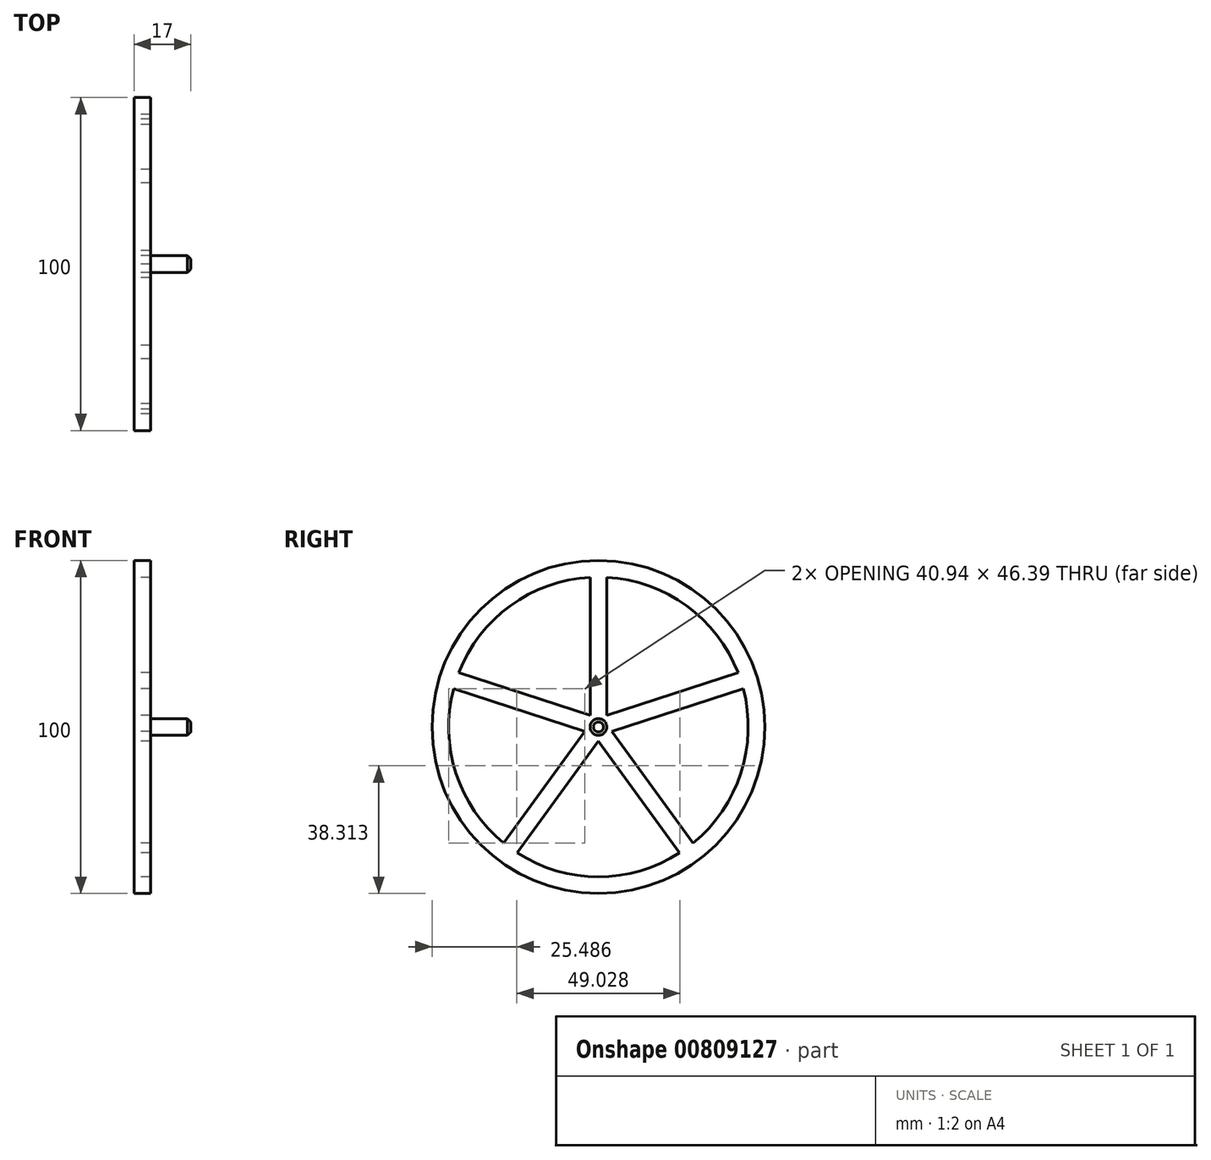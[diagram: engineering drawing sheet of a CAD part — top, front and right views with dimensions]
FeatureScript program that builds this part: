
annotation { "Feature Type Name" : "Feature", "Feature Type Description" : "" }
export const myFeature = defineFeature(function(context is Context, id is Id, definition is map)
    precondition{}
    {
        {
            var Q0;
            Q0=qCreatedBy(makeId("Right.planeOp"),FACE);
            var sketch = newSketch(context, id + "F0", { "sketchPlane" : qUnion([Q0])});
            skCircle(sketch, "E0", {"center": v(0, 0) * mm, "radius": 50 * mm});
            skCircle(sketch, "E1", {"center": v(0, 0) * mm, "radius": 5 * mm});
            skCircle(sketch, "E2", {"center": v(0, 0) * mm, "radius": 45 * mm});
            skLineSegment(sketch, "E3", {"start": v(-2.5, 0) * mm, "end": v(-2.5, 44.93) * mm});
            skLineSegment(sketch, "E4", {"start": v(2.5, 0) * mm, "end": v(2.5, 44.93) * mm});
            skLineSegment(sketch, "E5", {"start": v(-2.5, 0) * mm, "end": v(2.5, 0) * mm, "construction": true});
            skLineSegment(sketch, "E6.1.0", {"start": v(-0.77, -2.38) * mm, "end": v(-43.5, 11.5) * mm});
            skLineSegment(sketch, "E6.1.1", {"start": v(0.77, 2.38) * mm, "end": v(-41.96, 16.26) * mm});
            skLineSegment(sketch, "E6.2.0", {"start": v(2.02, -1.47) * mm, "end": v(-24.39, -37.82) * mm});
            skLineSegment(sketch, "E6.2.1", {"start": v(-2.02, 1.47) * mm, "end": v(-28.43, -34.88) * mm});
            skLineSegment(sketch, "E6.3.0", {"start": v(2.02, 1.47) * mm, "end": v(28.43, -34.88) * mm});
            skLineSegment(sketch, "E6.3.1", {"start": v(-2.02, -1.47) * mm, "end": v(24.39, -37.82) * mm});
            skLineSegment(sketch, "E6.4.0", {"start": v(-0.77, 2.38) * mm, "end": v(41.96, 16.26) * mm});
            skLineSegment(sketch, "E6.4.1", {"start": v(0.77, -2.38) * mm, "end": v(43.5, 11.5) * mm});
            skSolve(sketch);
        }
        {
            var Q0;
            {var subQ0=sQuery(id+"F0.wireOp",EDGE,"E4");var subQ1=sQuery(id+"F0.wireOp",EDGE,"E1");var subQ2=makeQuery(id+"F0.imprint","INTERSECT",VERTEX,{"derivedFrom":[subQ1,subQ0]});Q0=makeQuery(id+"F0.imprint","IMPRINT",FACE,{"disambiguationData":[TD([[makeQuery(id+"F0.imprint","IMPRINT",EDGE,{"disambiguationData":[TD([[subQ2,-1.0]])],"derivedFrom":subQ1}),-1.0]])]});}
            var Q1;
            {var subQ0=sQuery(id+"F0.wireOp",EDGE,"E6.1.1");var subQ1=sQuery(id+"F0.wireOp",EDGE,"E1");var subQ2=makeQuery(id+"F0.imprint","INTERSECT",VERTEX,{"derivedFrom":[subQ1,subQ0]});Q1=makeQuery(id+"F0.imprint","IMPRINT",FACE,{"disambiguationData":[TD([[makeQuery(id+"F0.imprint","IMPRINT",EDGE,{"disambiguationData":[TD([[subQ2,-1.0]])],"derivedFrom":subQ1}),-1.0]])]});}
            var Q2;
            {var subQ0=sQuery(id+"F0.wireOp",EDGE,"E6.2.1");var subQ1=sQuery(id+"F0.wireOp",EDGE,"E1");var subQ2=makeQuery(id+"F0.imprint","INTERSECT",VERTEX,{"derivedFrom":[subQ1,subQ0]});Q2=makeQuery(id+"F0.imprint","IMPRINT",FACE,{"disambiguationData":[TD([[makeQuery(id+"F0.imprint","IMPRINT",EDGE,{"disambiguationData":[TD([[subQ2,-1.0]])],"derivedFrom":subQ1}),-1.0]])]});}
            var Q3;
            {var subQ0=sQuery(id+"F0.wireOp",EDGE,"E6.3.1");var subQ1=sQuery(id+"F0.wireOp",EDGE,"E1");var subQ2=makeQuery(id+"F0.imprint","INTERSECT",VERTEX,{"derivedFrom":[subQ1,subQ0]});Q3=makeQuery(id+"F0.imprint","IMPRINT",FACE,{"disambiguationData":[TD([[makeQuery(id+"F0.imprint","IMPRINT",EDGE,{"disambiguationData":[TD([[subQ2,-1.0]])],"derivedFrom":subQ1}),-1.0]])]});}
            var Q4;
            {var subQ0=sQuery(id+"F0.wireOp",EDGE,"E6.4.0");var subQ1=sQuery(id+"F0.wireOp",EDGE,"E1");var subQ2=makeQuery(id+"F0.imprint","INTERSECT",VERTEX,{"derivedFrom":[subQ1,subQ0]});Q4=makeQuery(id+"F0.imprint","IMPRINT",FACE,{"disambiguationData":[TD([[makeQuery(id+"F0.imprint","IMPRINT",EDGE,{"disambiguationData":[TD([[subQ2,1.0]])],"derivedFrom":subQ1}),-1.0]])]});}
            var Q5;
            Q5=makeQuery(id+"F0.imprint","IMPRINT",FACE,{"disambiguationData":[TD([[makeQuery(id+"F0.imprint","IMPRINT",EDGE,{"derivedFrom":sQuery(id+"F0.wireOp",EDGE,"E0")}),1.0]])]});
            var Q6;
            {var subQ5=sQuery(id+"F0.wireOp",EDGE,"E4");var subQ6=sQuery(id+"F0.wireOp",EDGE,"E1");var subQ7=makeQuery(id+"F0.imprint","INTERSECT",VERTEX,{"derivedFrom":[subQ6,subQ5]});Q6=makeQuery(id+"F0.imprint","IMPRINT",FACE,{"disambiguationData":[TD([[makeQuery(id+"F0.imprint","IMPRINT",EDGE,{"disambiguationData":[TD([[subQ7,-1.0]])],"derivedFrom":subQ6}),1.0]])]});}
            var Q7;
            {var subQ1=sQuery(id+"F0.wireOp",EDGE,"E1");var subQ5=sQuery(id+"F0.wireOp",EDGE,"E6.1.1");var subQ6=makeQuery(id+"F0.imprint","INTERSECT",VERTEX,{"derivedFrom":[subQ1,subQ5]});Q7=makeQuery(id+"F0.imprint","IMPRINT",FACE,{"disambiguationData":[TD([[makeQuery(id+"F0.imprint","IMPRINT",EDGE,{"disambiguationData":[TD([[subQ6,-1.0]])],"derivedFrom":subQ1}),1.0]])]});}
            var Q8;
            {var subQ1=sQuery(id+"F0.wireOp",EDGE,"E1");var subQ5=sQuery(id+"F0.wireOp",EDGE,"E6.2.1");var subQ6=makeQuery(id+"F0.imprint","INTERSECT",VERTEX,{"derivedFrom":[subQ1,subQ5]});Q8=makeQuery(id+"F0.imprint","IMPRINT",FACE,{"disambiguationData":[TD([[makeQuery(id+"F0.imprint","IMPRINT",EDGE,{"disambiguationData":[TD([[subQ6,-1.0]])],"derivedFrom":subQ1}),1.0]])]});}
            var Q9;
            {var subQ1=sQuery(id+"F0.wireOp",EDGE,"E1");var subQ5=sQuery(id+"F0.wireOp",EDGE,"E6.3.1");var subQ6=makeQuery(id+"F0.imprint","INTERSECT",VERTEX,{"derivedFrom":[subQ1,subQ5]});Q9=makeQuery(id+"F0.imprint","IMPRINT",FACE,{"disambiguationData":[TD([[makeQuery(id+"F0.imprint","IMPRINT",EDGE,{"disambiguationData":[TD([[subQ6,-1.0]])],"derivedFrom":subQ1}),1.0]])]});}
            var Q10;
            {var subQ0=sQuery(id+"F0.wireOp",EDGE,"E6.4.0");var subQ1=sQuery(id+"F0.wireOp",EDGE,"E1");var subQ2=makeQuery(id+"F0.imprint","INTERSECT",VERTEX,{"derivedFrom":[subQ1,subQ0]});Q10=makeQuery(id+"F0.imprint","IMPRINT",FACE,{"disambiguationData":[TD([[makeQuery(id+"F0.imprint","IMPRINT",EDGE,{"disambiguationData":[TD([[subQ2,1.0]])],"derivedFrom":subQ1}),1.0]])]});}
            var Q11;
            {var subQ3=sQuery(id+"F0.wireOp",EDGE,"E3");var subQ8=sQuery(id+"F0.wireOp",EDGE,"E6.2.1");var subQ14=makeQuery(id+"F0.imprint","INTERSECT",VERTEX,{"derivedFrom":[subQ3,subQ8]});Q11=makeQuery(id+"F0.imprint","IMPRINT",FACE,{"disambiguationData":[TD([[makeQuery(id+"F0.imprint","IMPRINT",EDGE,{"disambiguationData":[TD([[subQ14,-1.0]])],"derivedFrom":subQ3}),-1.0]])]});}
            extrude(context, id + "F1", {"entities" : qUnion([Q0, Q1, Q2, Q3, Q4, Q5, Q6, Q7, Q8, Q9, Q10, Q11]), "endBound" : BoundingType.SYMMETRIC, "depth" : 5 * mm, "offsetDistance" : 25.4 * mm});
        }
        {
            var Q0;
            Q0=makeQuery(id+"F1.opExtrude","CAP_FACE",FACE,{"disambiguationData":[OSD([sQuery(id+"F0.wireOp",EDGE,"E0")])],"isStart":false});
            var sketch = newSketch(context, id + "F2", { "sketchPlane" : qUnion([Q0])});
            skCircle(sketch, "E7", {"center": v(0, 0) * mm, "radius": 2.5 * mm});
            skSolve(sketch);
        }
        {
            var Q0;
            Q0=qSketchRegion(id+"F2",true);
            extrude(context, id + "F3", {"entities" : qUnion([Q0]), "operationType" : NewBodyOperationType.ADD, "depth" : 12 * mm, "offsetDistance" : 25.4 * mm});
        }
        {
            var Q0;
            {var subQ0=sQuery(id+"F2.wireOp",EDGE,"E7");Q0=makeQuery(id+"FSZQR90olkzr3mr_1.boolean.opBoolean","SPLIT",EDGE,{"disambiguationData":[TD([makeQuery(id+"FSZQR90olkzr3mr_1.opExtrude","SWEPT_FACE",FACE,{"disambiguationData":[OSD([sQuery(id+"FjNn55fEC51aYcL_1.wireOp",EDGE,"ETVrjkb7-6Fxv-ITG9-y2zV-0GoN309nHeMa.bottom")])]})])],"derivedFrom":makeQuery(id+"F3.opExtrude","CAP_EDGE",EDGE,{"disambiguationData":[OSD([subQ0])],"isStart":false})});}
            chamfer(context, id + "F4", {"entities" : qUnion([Q0]), "width" : 1 * mm, "tangentPropagation" : true});
        }
    });
